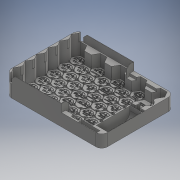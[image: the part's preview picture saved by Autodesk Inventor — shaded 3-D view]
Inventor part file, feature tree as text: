
AUTODESK INVENTOR PART (.ipt)
format: ipt  version: 2018 (Build 220112000, 112)  size: 14,822,912 bytes
history: native  units: mm
features: projected_geometry x24, extrude x21, sketch x19, pattern_linear x4, fillet x3, chamfer x1
ambient origin geometry x8: Origin, YZ Plane, XZ Plane, XY Plane, X Axis, Y Axis, Z Axis, Center Point
bodies: Body1 (feature_tree)
feature tree (72):
  extrude  "Extrusion11"  Depth=35.5mm
  extrude  "Extrusion12"  Depth=10.0mm
  sketch  "Sketch14"  dims[d80=0.2mm d118=20.0mm d120=36.5mm]
  extrude  "Extrusion13"  Depth=36.5mm
  extrude  "Extrusion14"  Depth=50.0mm
  sketch  "Sketch15"  dims[d121=10.0mm d123=10.0mm d125=50.0mm d127=63.219854mm]
  extrude  "Extrusion15"  Depth=38.0mm TaperAngle=0.0deg
  extrude  "Extrusion16"  Depth=36.5mm
  extrude  "Extrusion17"  Depth=36.5mm
  fillet  "Fillet2"  Radius=10.0mm
  extrude  "Extrusion18"  Depth=10.0mm
  extrude  "Extrusion19"  Depth=0.5mm TaperAngle=0.0deg
  extrude  "Extrusion20"  Depth=227.899911mm
  chamfer  "Chamfer1"  Distance=36.5mm
  extrude  "Extrusion21"  Depth=10.0mm TaperAngle=0.0deg
  extrude  "Extrusion22"  Depth=41.0mm
  fillet  "Fillet3"  Radius=8.5mm
  extrude  "Extrusion23"  Depth=37.0mm
  extrude  "Extrusion24"  Depth=24.0mm
  extrude  "Extrusion25"  Depth=1.0mm
  extrude  "Extrusion26"  Depth=4.0mm
  extrude  "Extrusion27"  Depth=33.0mm TaperAngle=0.0deg
  pattern_linear  "Rectangular Pattern2"  Spacing1=223.0mm  [1 undecoded]
  pattern_linear  "Rectangular Pattern3"  Spacing1=1.0mm  [1 undecoded]
  extrude  "Extrusion28"  Depth=30.0mm
  extrude  "Extrusion29"  Depth=1.249955mm
  fillet  "Fillet4"  Radius=1.249955mm
  extrude  "Extrusion31"  Depth=1.0mm
  pattern_linear  "Rectangular Pattern4"  Spacing1=1.0mm  [1 undecoded]
  extrude  "Extrusion32"  Depth=1.0mm
  pattern_linear  "Rectangular Pattern5"  Spacing1=1.249955mm  [1 undecoded]
  sketch  "Sketch1"  dims[d2=35.5mm d23=18.288mm]
  sketch  "Sketch13"  dims[d24=60.0mm d26=36.5mm d27=10.0mm d29=10.0mm]
  projected_geometry  "Projected Loop14"
  projected_geometry  "Projected Loop15"
  projected_geometry  "Projected Loop16"
  projected_geometry  "Projected Loop17"
  projected_geometry  "Projected Loop18"
  projected_geometry  "Projected Loop19"
  projected_geometry  "Projected Loop20"
  projected_geometry  "Projected Loop21"
  projected_geometry  "Projected Loop22"
  sketch  "Sketch16"  dims[d128=10.0mm d130=10.0mm d133=38.0mm d134=1.0mm d135=0.0mm d136=0.0mm]
  projected_geometry  "Projected Loop23"
  sketch  "Sketch17"  dims[d137=1.0mm d138=0.0mm d139=60.0mm d141=36.5mm]
  projected_geometry  "Projected Loop24"
  sketch  "Sketch18"  dims[d142=10.0mm d144=10.0mm d146=20.0mm d148=36.5mm d149=10.0mm d151=10.0mm]
  projected_geometry  "Projected Loop25"
  sketch  "Sketch19"  dims[d153=40.0mm d155=63.219854mm d156=10.0mm d158=10.0mm]
  projected_geometry  "Projected Loop26"
  sketch  "Sketch20"  dims[d160=0.5mm d161=0.0mm d162=0.5mm d163=0.0mm]
  projected_geometry  "Projected Loop27"
  sketch  "Sketch21"  dims[d164=301.559911mm d165=227.899911mm]
  projected_geometry  "Projected Loop28"
  sketch  "Sketch22"  dims[d166=128.0mm d167=20.0mm d169=36.5mm]
  projected_geometry  "Projected Loop29"
  sketch  "Sketch23"  dims[d170=10.0mm d172=10.0mm d174=0.5mm d175=0.0mm]
  projected_geometry  "Projected Loop30"
  sketch  "Sketch24"  dims[d176=0.5mm d177=0.0mm d179=41.0mm d180=8.5mm]
  projected_geometry  "Projected Loop31"
  sketch  "Sketch25"  dims[d181=15.0mm d182=37.0mm]
  projected_geometry  "Projected Loop32"
  sketch  "Sketch26"  dims[d183=33.5mm d184=24.0mm]
  projected_geometry  "Projected Loop33"
  sketch  "Sketch27"  dims[d185=32.0mm d186=1.0mm]
  projected_geometry  "Projected Loop34"
  sketch  "Sketch29"  dims[d187=0.5mm d188=0.0mm d189=4.0mm]
  projected_geometry  "Projected Loop35"
  sketch  "Sketch32"  dims[d190=0.5mm d191=0.0mm d192=33.0mm d193=0.0mm]
  projected_geometry  "Projected Loop36"
  sketch  "Sketch33"  dims[d194=162.0mm d195=223.0mm d196=1.0mm d197=139.0mm d198=1.249955mm d199=1.249955mm d200=1.0mm d201=1.0mm d202=1.0mm d203=1.249955mm d204=24.5mm d205=0.0mm d206=10.0mm d207=2.0mm d208=45.0deg d209=199.6mm d210=82.4mm d211=84.5mm d212=201.6mm d213=8.0mm d214=0.0mm d215=35.898551mm d216=106.0mm d217=1.0mm d218=36.5mm d219=0.0mm d220=25.0mm d222=16.0mm d223=10.0mm d224=80.0mm d226=31.609927mm d227=10.0mm d229=10.0mm d231=3.0mm d232=0.0mm d233=16.0mm d234=10.0mm d235=3.0mm d236=0.0mm d237=16.0mm d238=10.0mm d239=3.0mm d240=0.0mm d241=16.0mm d242=10.0mm d243=3.0mm d244=0.0mm d245=16.0mm d246=10.0mm d247=3.0mm d248=0.0mm d249=50.0mm d251=36.5mm d252=40.0mm d254=63.219854mm d255=50.0mm d257=36.5mm d258=30.0mm d260=63.219854mm d261=16.0mm d262=10.0mm d263=3.0mm d264=0.0mm d266=1.0mm d267=1.0mm d268=58.0mm d269=10.0mm d270=1.474978mm d271=1.474978mm d272=52.0mm d273=10.0mm d274=0.0mm d275=29.0mm d281=10.0mm d282=0.0mm d283=60.0mm d285=36.5mm d286=40.0mm d288=63.219854mm d289=10.0mm d290=0.0mm d291=50.0mm d293=36.5mm d294=30.0mm d296=63.219854mm]
  projected_geometry  "Projected Loop37"
note: 4 required parameter values undecoded (feature->parameter linkage not recoverable at this tier; creation-order binding heuristic only, values carry confidence <= 0.55)
